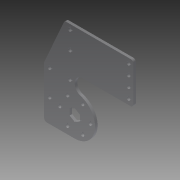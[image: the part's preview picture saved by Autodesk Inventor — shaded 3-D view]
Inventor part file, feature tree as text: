
AUTODESK INVENTOR PART (.ipt)
format: ipt  version: 2014 (Build 180170000, 170)  size: 156,160 bytes
history: native  units: in
note: dims shown in document units (in); Inventor stores cm internally (conversion verified against a paired STEP export)
features: extrude x1, fillet x1
ambient origin geometry x8: Origin, YZ Plane, XZ Plane, XY Plane, X Axis, Y Axis, Z Axis, Center Point
bodies: Solid1 (feature_tree)
feature tree (2):
  extrude  "Extrusion1"  Depth=0.125in TaperAngle=0.0deg
  fillet  "Fillet1"  Radius=0.625in
